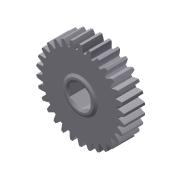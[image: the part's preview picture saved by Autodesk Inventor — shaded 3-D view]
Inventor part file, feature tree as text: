
AUTODESK INVENTOR PART (.ipt)
format: ipt  version: 2015 (Build 190159000, 159)  size: 313,344 bytes
history: native  units: mm (DEFAULTED — no unit token found)
features: sketch x5, extrude x3, plane x3, other x3, revolve x1, projected_geometry x1
ambient origin geometry x8: Origin, YZ Plane, XZ Plane, XY Plane, X Axis, Y Axis, Z Axis, Center Point
bodies: Solid1 (feature_tree)
feature tree (16):
  extrude  "Extrusion1"  Depth=9.525mm TaperAngle=0.0deg
  plane  "Work Plane1"
  plane  "Work Plane2"
  plane  "Work Plane3"
  other  "Spur Gear"
  extrude  "Extrusion2"  Depth=76.2mm TaperAngle=0.0deg
  extrude  "Extrusion3"  TaperAngle=0.0deg  [1 undecoded]
  revolve  "Revolution1"  [1 undecoded]
  sketch  "Sketch1"  dims[d0=40.64mm d1=9.525mm d2=0.0mm]
  sketch  "Sketch2"  dims[d3=38.1mm d4=76.2mm d5=0.0mm]
  other  "Srf1"
  sketch  "Sketch3"  dims[d6=0.0mm d7=1.047198mm d9=0.0mm]
  sketch  "Sketch4"  dims[d14=0.0mm d15=95.25mm d16=0.0mm]
  sketch  "Sketch5"  dims[d17=0.0mm d18=0.0mm d19=95.25mm d20=15.9004mm d21=0.635mm d22=0.0mm d23=9.525mm d24=0.635mm d25=0.0mm d26=1.143mm d27=0.889mm d28=5.070181mm d29=2.54mm d30=90.0deg]
  other  "Pitch Diameter"
  projected_geometry  "Project Cut Edges1"
note: 2 required parameter values undecoded (feature->parameter linkage not recoverable at this tier; creation-order binding heuristic only, values carry confidence <= 0.55)